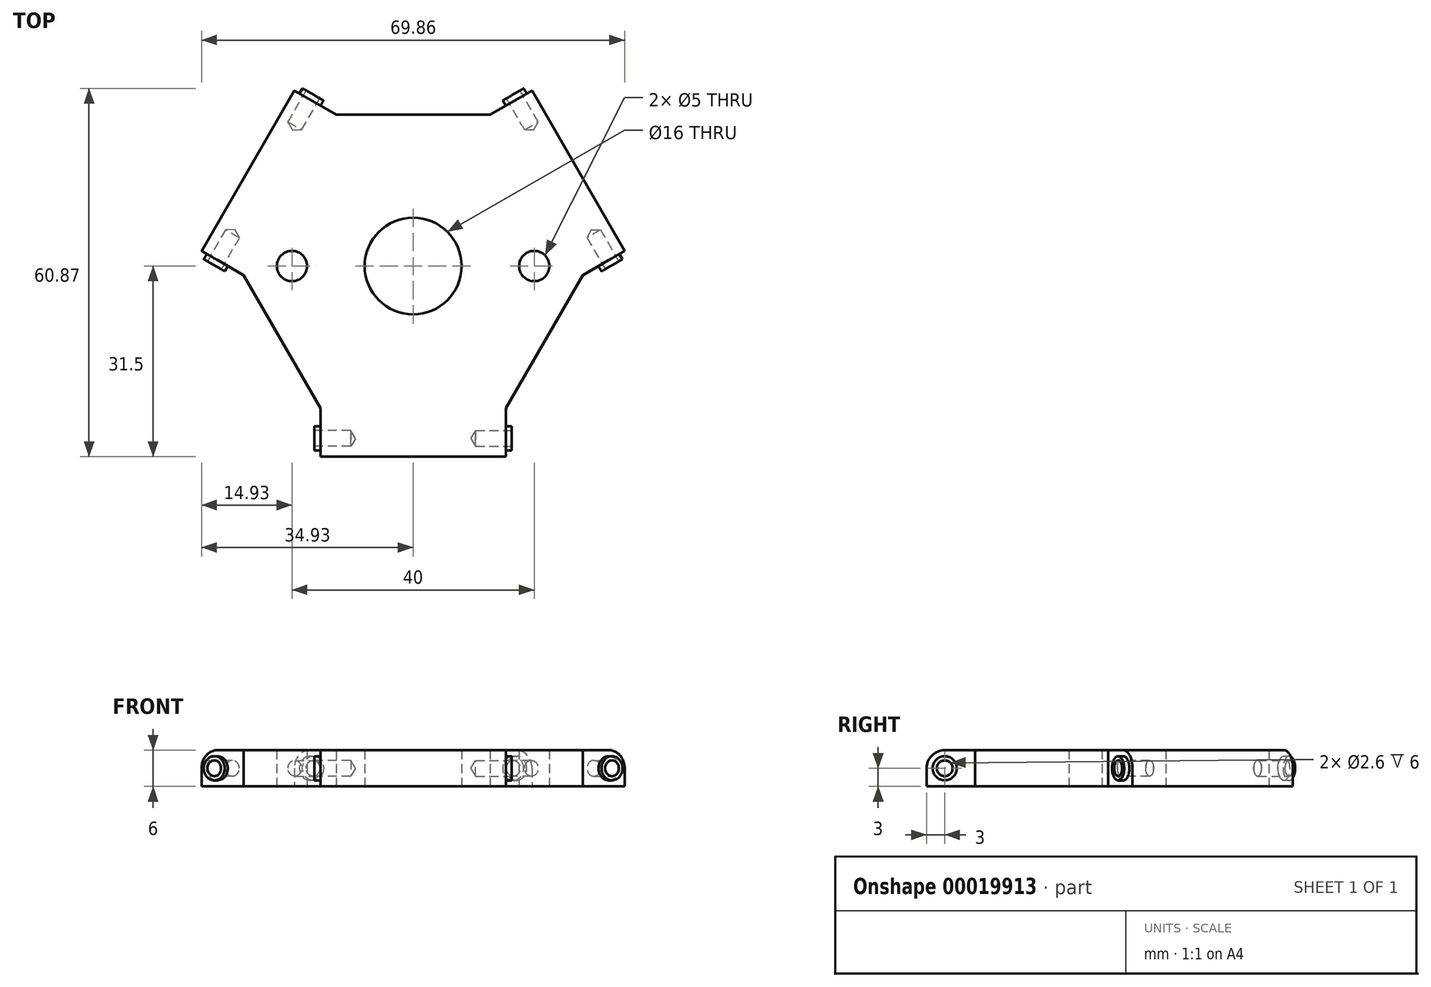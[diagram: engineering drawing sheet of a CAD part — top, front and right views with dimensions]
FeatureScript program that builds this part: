
annotation { "Feature Type Name" : "Feature", "Feature Type Description" : "" }
export const myFeature = defineFeature(function(context is Context, id is Id, definition is map)
    precondition{}
    {
        {
            var Q0;
            Q0=qCreatedBy(makeId("Top.planeOp"),FACE);
            var sketch = newSketch(context, id + "F0", { "sketchPlane" : qUnion([Q0])});
            skLineSegment(sketch, "E0", {"start": v(0, 0) * mm, "end": v(0, 25) * mm, "construction": true});
            skLineSegment(sketch, "E1", {"start": v(0, 0) * mm, "end": v(21.65, -12.5) * mm, "construction": true});
            skLineSegment(sketch, "E2", {"start": v(0, 0) * mm, "end": v(-21.65, -12.5) * mm, "construction": true});
            skCircle(sketch, "E3", {"center": v(0, 0) * mm, "radius": 8 * mm});
            skPoint(sketch, "E4.visualSharp", {"position": v(0, 25) * mm});
            skLineSegment(sketch, "E5", {"start": v(-12.7, 25) * mm, "end": v(-19.63, 29) * mm});
            skLineSegment(sketch, "E6", {"start": v(-19.63, 29) * mm, "end": v(-34.93, 2.5) * mm});
            skLineSegment(sketch, "E7", {"start": v(-34.93, 2.5) * mm, "end": v(-28, -1.5) * mm});
            skLineSegment(sketch, "E8", {"start": v(-15.3, -23.5) * mm, "end": v(-15.3, -31.5) * mm});
            skLineSegment(sketch, "E9", {"start": v(-15.3, -31.5) * mm, "end": v(15.3, -31.5) * mm});
            skLineSegment(sketch, "E10", {"start": v(15.3, -31.5) * mm, "end": v(15.3, -23.5) * mm});
            skLineSegment(sketch, "E11", {"start": v(28, -1.5) * mm, "end": v(34.93, 2.5) * mm});
            skLineSegment(sketch, "E12", {"start": v(34.93, 2.5) * mm, "end": v(19.63, 29) * mm});
            skLineSegment(sketch, "E13", {"start": v(19.63, 29) * mm, "end": v(12.7, 25) * mm});
            skLineSegment(sketch, "E14", {"start": v(0, 0) * mm, "end": v(-27.28, 15.75) * mm, "construction": true});
            skLineSegment(sketch, "E15", {"start": v(0, 0) * mm, "end": v(0, -31.5) * mm, "construction": true});
            skLineSegment(sketch, "E16", {"start": v(0, 0) * mm, "end": v(27.28, 15.75) * mm, "construction": true});
            skLineSegment(sketch, "E17", {"start": v(-12.7, 25) * mm, "end": v(12.7, 25) * mm});
            skLineSegment(sketch, "E18", {"start": v(28, -1.5) * mm, "end": v(15.3, -23.5) * mm});
            skLineSegment(sketch, "E19", {"start": v(-28, -1.5) * mm, "end": v(-15.3, -23.5) * mm});
            skCircle(sketch, "E20", {"center": v(-20, 0) * mm, "radius": 2.5 * mm});
            skCircle(sketch, "E21", {"center": v(20, 0) * mm, "radius": 2.5 * mm});
            skSolve(sketch);
        }
        {
            var Q0;
            Q0 = qSketchRegion(id + "F0", true);
            extrude(context, id + "F1", {"entities" : qUnion([Q0]), "depth" : 3 * mm, "hasSecondDirection" : true, "secondDirectionOppositeDirection" : true, "secondDirectionDepth" : 3 * mm});
        }
        {
            var Q0;
            Q0=makeQuery(id+"F1.opExtrude","SWEPT_FACE",FACE,{"disambiguationData":[OSD([sQuery(id+"F0.wireOp",EDGE,"E8")])]});
            var sketch = newSketch(context, id + "F2", { "sketchPlane" : qUnion([Q0])});
            skCircle(sketch, "E22", {"center": v(28.5, 0) * mm, "radius": 2 * mm});
            skSolve(sketch);
        }
        {
            var Q0;
            Q0 = qSketchRegion(id + "F2", true);
            extrude(context, id + "F3", {"entities" : qUnion([Q0]), "depth" : 1 * mm});
        }
        {
            var Q0;
            Q0=makeQuery(id+"F3.opExtrude","CAP_FACE",FACE,{"disambiguationData":[OSD([sQuery(id+"F2.wireOp",EDGE,"E22")])],"isStart":false});
            var sketch = newSketch(context, id + "F4", { "sketchPlane" : qUnion([Q0])});
            skPoint(sketch, "E23", {"position": v(28.5, 0) * mm});
            skSolve(sketch);
        }
        {
            var Q0;
            Q0=makeQuery(id+"F3.opExtrude","SWEPT_BODY",BODY,{"disambiguationData":[OSD([sQuery(id+"F2.wireOp",EDGE,"E22")])]});
            var Q1;
            Q1=qCreatedBy(makeId("Right.planeOp"),FACE);
            mirror(context, id + "F5", {"entities" : qUnion([Q0]), "mirrorPlane" : qUnion([Q1])});
        }
        {
            var Q0;
            Q0=makeQuery(id+"F3.opExtrude","SWEPT_BODY",BODY,{"disambiguationData":[OSD([sQuery(id+"F2.wireOp",EDGE,"E22")])]});
            var Q1;
            Q1=makeQuery(id+"F5.opPattern","COPY",BODY,{"derivedFrom":makeQuery(id+"F3.opExtrude","SWEPT_BODY",BODY,{"disambiguationData":[OSD([sQuery(id+"F2.wireOp",EDGE,"E22")])]}),"instanceName":"1"});
            var Q2;
            Q2=makeQuery(id+"F1.opExtrude","SWEPT_FACE",FACE,{"disambiguationData":[OSD([sQuery(id+"F0.wireOp",EDGE,"E3")])]});
            circularPattern(context, id + "F6", {"operationType" : NewBodyOperationType.ADD, "entities" : qUnion([Q0, Q1]), "axis" : qUnion([Q2]), "angle" : 120 * degree, "instanceCount" : 3});
        }
        {
            var Q0;
            Q0=makeQuery(id+"F5.opPattern","COPY",FACE,{"derivedFrom":makeQuery(id+"F3.opExtrude","CAP_FACE",FACE,{"disambiguationData":[OSD([sQuery(id+"F2.wireOp",EDGE,"E22")])],"isStart":false}),"instanceName":"1"});
            var sketch = newSketch(context, id + "F7", { "sketchPlane" : qUnion([Q0])});
            skPoint(sketch, "E24", {"position": v(-28.5, 0) * mm});
            skSolve(sketch);
        }
        {
            var Q0;
            Q0=makeQuery(id+"F6.opPattern","COPY",FACE,{"derivedFrom":makeQuery(id+"F3.opExtrude","CAP_FACE",FACE,{"disambiguationData":[OSD([sQuery(id+"F2.wireOp",EDGE,"E22")])],"isStart":false}),"instanceName":"1"});
            var sketch = newSketch(context, id + "F8", { "sketchPlane" : qUnion([Q0])});
            skPoint(sketch, "E25", {"position": v(28.5, 0) * mm});
            skSolve(sketch);
        }
        {
            var Q0;
            Q0=makeQuery(id+"F6.opPattern","COPY",FACE,{"derivedFrom":makeQuery(id+"F5.opPattern","COPY",FACE,{"derivedFrom":makeQuery(id+"F3.opExtrude","CAP_FACE",FACE,{"disambiguationData":[OSD([sQuery(id+"F2.wireOp",EDGE,"E22")])],"isStart":false}),"instanceName":"1"}),"instanceName":"1"});
            var sketch = newSketch(context, id + "F9", { "sketchPlane" : qUnion([Q0])});
            skPoint(sketch, "E26", {"position": v(-28.5, 0) * mm});
            skSolve(sketch);
        }
        {
            var Q0;
            Q0=makeQuery(id+"F6.opPattern","COPY",FACE,{"derivedFrom":makeQuery(id+"F3.opExtrude","CAP_FACE",FACE,{"disambiguationData":[OSD([sQuery(id+"F2.wireOp",EDGE,"E22")])],"isStart":false}),"instanceName":"2"});
            var sketch = newSketch(context, id + "F10", { "sketchPlane" : qUnion([Q0])});
            skPoint(sketch, "E27", {"position": v(28.5, 0) * mm});
            skSolve(sketch);
        }
        {
            var Q0;
            Q0=makeQuery(id+"F6.opPattern","COPY",FACE,{"derivedFrom":makeQuery(id+"F5.opPattern","COPY",FACE,{"derivedFrom":makeQuery(id+"F3.opExtrude","CAP_FACE",FACE,{"disambiguationData":[OSD([sQuery(id+"F2.wireOp",EDGE,"E22")])],"isStart":false}),"instanceName":"1"}),"instanceName":"2"});
            var sketch = newSketch(context, id + "F11", { "sketchPlane" : qUnion([Q0])});
            skPoint(sketch, "E28", {"position": v(-28.5, 0) * mm});
            skSolve(sketch);
        }
        {
            var Q0;
            Q0=sQuery(id+"F9.wireOp",VERTEX,"E26");
            var Q1;
            Q1=sQuery(id+"F10.wireOp",VERTEX,"E27");
            var Q2;
            Q2=sQuery(id+"F11.wireOp",VERTEX,"E28");
            var Q3;
            Q3=sQuery(id+"F4.wireOp",VERTEX,"E23");
            var Q4;
            Q4=sQuery(id+"F7.wireOp",VERTEX,"E24");
            var Q5;
            Q5=sQuery(id+"F8.wireOp",VERTEX,"E25");
            var Q6;
            Q6=makeQuery(id+"F6.opPattern","COPY",BODY,{"derivedFrom":makeQuery(id+"F5.opPattern","COPY",BODY,{"derivedFrom":makeQuery(id+"F3.opExtrude","SWEPT_BODY",BODY,{"disambiguationData":[OSD([sQuery(id+"F2.wireOp",EDGE,"E22")])]}),"instanceName":"1"}),"instanceName":"1"});
            var Q7;
            Q7=makeQuery(id+"F6.opPattern","COPY",BODY,{"derivedFrom":makeQuery(id+"F3.opExtrude","SWEPT_BODY",BODY,{"disambiguationData":[OSD([sQuery(id+"F2.wireOp",EDGE,"E22")])]}),"instanceName":"2"});
            var Q8;
            Q8=makeQuery(id+"F6.opPattern","COPY",BODY,{"derivedFrom":makeQuery(id+"F5.opPattern","COPY",BODY,{"derivedFrom":makeQuery(id+"F3.opExtrude","SWEPT_BODY",BODY,{"disambiguationData":[OSD([sQuery(id+"F2.wireOp",EDGE,"E22")])]}),"instanceName":"1"}),"instanceName":"2"});
            var Q9;
            Q9=makeQuery(id+"F3.opExtrude","SWEPT_BODY",BODY,{"disambiguationData":[OSD([sQuery(id+"F2.wireOp",EDGE,"E22")])]});
            var Q10;
            Q10=makeQuery(id+"F5.opPattern","COPY",BODY,{"derivedFrom":makeQuery(id+"F3.opExtrude","SWEPT_BODY",BODY,{"disambiguationData":[OSD([sQuery(id+"F2.wireOp",EDGE,"E22")])]}),"instanceName":"1"});
            var Q11;
            Q11=makeQuery(id+"F6.opPattern","COPY",BODY,{"derivedFrom":makeQuery(id+"F3.opExtrude","SWEPT_BODY",BODY,{"disambiguationData":[OSD([sQuery(id+"F2.wireOp",EDGE,"E22")])]}),"instanceName":"1"});
            var Q12;
            Q12=makeQuery(id+"F1.opExtrude","SWEPT_BODY",BODY,{"disambiguationData":[OSD([sQuery(id+"F0.wireOp",EDGE,"E3"),sQuery(id+"F0.wireOp",EDGE,"E5"),sQuery(id+"F0.wireOp",EDGE,"E6"),sQuery(id+"F0.wireOp",EDGE,"E7"),sQuery(id+"F0.wireOp",EDGE,"E8"),sQuery(id+"F0.wireOp",EDGE,"E9"),sQuery(id+"F0.wireOp",EDGE,"E10"),sQuery(id+"F0.wireOp",EDGE,"E11"),sQuery(id+"F0.wireOp",EDGE,"E12"),sQuery(id+"F0.wireOp",EDGE,"E13"),sQuery(id+"F0.wireOp",EDGE,"E17"),sQuery(id+"F0.wireOp",EDGE,"E18"),sQuery(id+"F0.wireOp",EDGE,"E19"),sQuery(id+"F0.wireOp",EDGE,"E20"),sQuery(id+"F0.wireOp",EDGE,"E21")])]});
            hole(context, id + "F12", {"style" : HoleStyle.SIMPLE, "holeDiameter" : 2.6 * mm, "endStyle" : HoleEndStyle.BLIND, "holeDepth" : 6 * mm, "locations" : qUnion([Q0, Q1, Q2, Q3, Q4, Q5]), "scope" : qUnion([Q6, Q7, Q8, Q9, Q10, Q11, Q12])});
        }
        {
            var Q0;
            Q0=makeQuery(id+"F1.opExtrude","CAP_EDGE",EDGE,{"disambiguationData":[OSD([sQuery(id+"F0.wireOp",EDGE,"E12")])],"isStart":false});
            var Q1;
            Q1=makeQuery(id+"F1.opExtrude","CAP_EDGE",EDGE,{"disambiguationData":[OSD([sQuery(id+"F0.wireOp",EDGE,"E6")])],"isStart":false});
            var Q2;
            Q2=makeQuery(id+"F1.opExtrude","CAP_EDGE",EDGE,{"disambiguationData":[OSD([sQuery(id+"F0.wireOp",EDGE,"E9")])],"isStart":false});
            fillet(context, id + "F13", {"entities" : qUnion([Q0, Q1, Q2]), "radius" : 3 * mm, "tangentPropagation" : true, "allowEdgeOverflow" : false});
        }
    });
